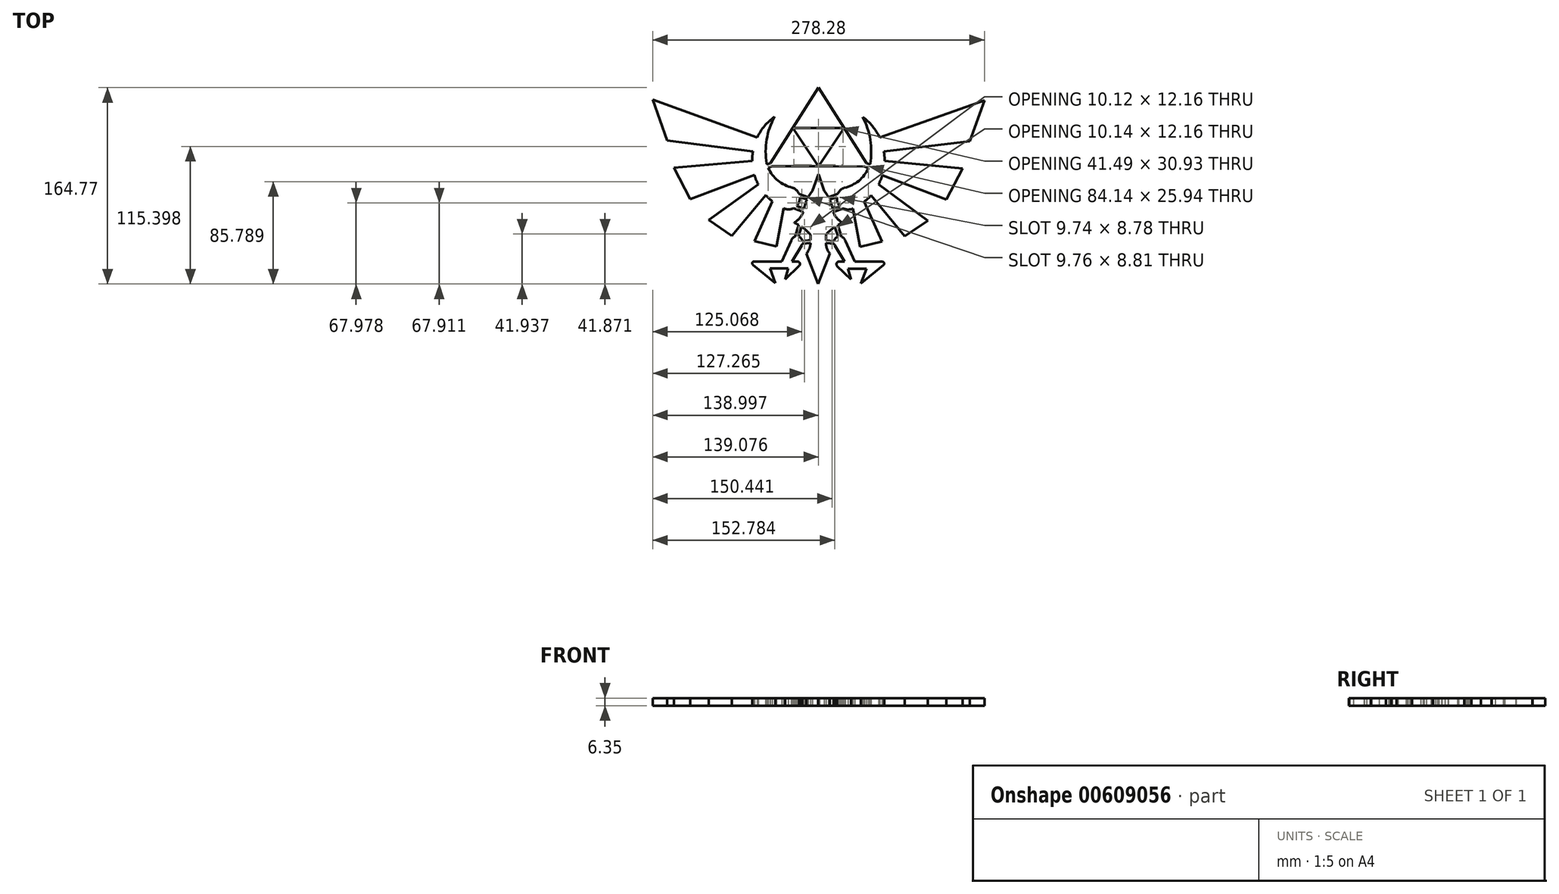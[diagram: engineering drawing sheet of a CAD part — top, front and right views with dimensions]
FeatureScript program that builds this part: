
annotation { "Feature Type Name" : "Feature", "Feature Type Description" : "" }
export const myFeature = defineFeature(function(context is Context, id is Id, definition is map)
    precondition{}
    {
        {
            var Q0;
            Q0=qCreatedBy(makeId("Top.planeOp"),FACE);
            var sketch = newSketch(context, id + "F0", { "sketchPlane" : qUnion([Q0])});
            skArc(sketch, "E0", {"start": v(-28.79, -20.12) * mm, "mid": v(-24.77, -21.01) * mm, "end": v(-20.76, -20.1) * mm});
            skLineSegment(sketch, "E1", {"start": v(-38.33, -14.34) * mm, "end": v(-53.53, -47.7) * mm});
            skLineSegment(sketch, "E2", {"start": v(-53.53, -47.7) * mm, "end": v(-35.08, -52.18) * mm});
            skLineSegment(sketch, "E3", {"start": v(-35.08, -52.18) * mm, "end": v(-28.79, -20.12) * mm});
            skLineSegment(sketch, "E4", {"start": v(-43.98, -9.01) * mm, "end": v(-72.5, -43.13) * mm});
            skLineSegment(sketch, "E5", {"start": v(-72.5, -43.13) * mm, "end": v(-91.8, -29.95) * mm});
            skLineSegment(sketch, "E6", {"start": v(-91.8, -29.95) * mm, "end": v(-50.28, 0.16) * mm});
            skLineSegment(sketch, "E7", {"start": v(-53.41, 7.92) * mm, "end": v(-107.23, -12.28) * mm});
            skLineSegment(sketch, "E8", {"start": v(-107.23, -12.28) * mm, "end": v(-120.85, 13.84) * mm});
            skLineSegment(sketch, "E9", {"start": v(-120.85, 13.84) * mm, "end": v(-55.26, 19.83) * mm});
            skLineSegment(sketch, "E10", {"start": v(-54.69, 27.79) * mm, "end": v(-126.62, 36.86) * mm});
            skLineSegment(sketch, "E11", {"start": v(-126.62, 36.86) * mm, "end": v(-138.76, 71.25) * mm});
            skLineSegment(sketch, "E12", {"start": v(-138.76, 71.25) * mm, "end": v(-51.03, 39.53) * mm});
            skArc(sketch, "E13", {"start": v(-36.63, 56.77) * mm, "mid": v(-44.94, 49.07) * mm, "end": v(-51.03, 39.53) * mm});
            skArc(sketch, "E14.trimOffspring", {"start": v(-54.69, 27.79) * mm, "mid": v(-55.16, 23.82) * mm, "end": v(-55.27, 19.83) * mm});
            skArc(sketch, "E15.trimOffspring", {"start": v(-53.44, 7.9) * mm, "mid": v(-52.06, 3.95) * mm, "end": v(-50.32, 0.14) * mm});
            skArc(sketch, "E16.trimOffspring", {"start": v(-44, -9.04) * mm, "mid": v(-41.29, -11.83) * mm, "end": v(-38.34, -14.37) * mm});
            skArc(sketch, "E17", {"start": v(-36.63, 56.77) * mm, "mid": v(-43.19, 37.67) * mm, "end": v(-43.16, 17.49) * mm});
            skArc(sketch, "E18", {"start": v(-43.16, 17.49) * mm, "mid": v(-43.09, 17.22) * mm, "end": v(-43, 16.96) * mm});
            skArc(sketch, "E19", {"start": v(-13.79, -50.98) * mm, "mid": v(-13.48, -50.39) * mm, "end": v(-13.26, -49.76) * mm});
            skLineSegment(sketch, "E20", {"start": v(-22.58, -47.14) * mm, "end": v(-30.59, -64.63) * mm});
            skLineSegment(sketch, "E21", {"start": v(-30.59, -64.63) * mm, "end": v(-53.76, -64.63) * mm});
            skLineSegment(sketch, "E22", {"start": v(-22.04, -64.63) * mm, "end": v(-17.52, -64.63) * mm});
            skLineSegment(sketch, "E23", {"start": v(-13.79, -50.98) * mm, "end": v(-22.04, -64.63) * mm});
            skArc(sketch, "E24", {"start": v(-53.47, -64.63) * mm, "mid": v(-55.2, -65.58) * mm, "end": v(-54.75, -67.5) * mm});
            skArc(sketch, "E25", {"start": v(-16.15, -68.69) * mm, "mid": v(-15.4, -66.17) * mm, "end": v(-17.52, -64.63) * mm});
            skLineSegment(sketch, "E26", {"start": v(-15.83, -68.38) * mm, "end": v(-27.53, -79.54) * mm});
            skLineSegment(sketch, "E27", {"start": v(-27.53, -79.54) * mm, "end": v(-25.03, -70.53) * mm});
            skLineSegment(sketch, "E28", {"start": v(-25.03, -70.53) * mm, "end": v(-40.41, -70.53) * mm});
            skLineSegment(sketch, "E29", {"start": v(-40.41, -70.53) * mm, "end": v(-35.86, -82.97) * mm});
            skLineSegment(sketch, "E30", {"start": v(-35.86, -82.97) * mm, "end": v(-54.75, -67.5) * mm});
            skLineSegment(sketch, "E31", {"start": v(0, 8.03) * mm, "end": v(-4.66, -5.48) * mm});
            skArc(sketch, "E32", {"start": v(-4.66, -5.48) * mm, "mid": v(-6.6, -8) * mm, "end": v(-8.28, -10.68) * mm});
            skArc(sketch, "E33", {"start": v(-20.17, -32.15) * mm, "mid": v(-15.52, -28.26) * mm, "end": v(-12.38, -23.07) * mm});
            skArc(sketch, "E34", {"start": v(-6.43, -42.15) * mm, "mid": v(-9.93, -38.58) * mm, "end": v(-13.88, -35.52) * mm});
            skArc(sketch, "E35", {"start": v(-9.73, -57.97) * mm, "mid": v(-7.47, -54.25) * mm, "end": v(-6.43, -50.01) * mm});
            skLineSegment(sketch, "E36", {"start": v(-6.43, -42.15) * mm, "end": v(-6.43, -46.8) * mm});
            skLineSegment(sketch, "E37", {"start": v(-9.73, -57.97) * mm, "end": v(0, -83.54) * mm});
            skLineSegment(sketch, "E38", {"start": v(-20.43, 46.05) * mm, "end": v(-0.78, 16.4) * mm});
            skLineSegment(sketch, "E39", {"start": v(0, 15.22) * mm, "end": v(-38.54, 15.22) * mm});
            skLineSegment(sketch, "E40", {"start": v(-40.13, 17.92) * mm, "end": v(-21.27, 47.32) * mm});
            skLineSegment(sketch, "E41", {"start": v(-21.27, 47.32) * mm, "end": v(0.4, 81.23) * mm});
            skLineSegment(sketch, "E42", {"start": v(-19.67, 47.32) * mm, "end": v(0, 47.32) * mm});
            skLineSegment(sketch, "E43", {"start": v(-16.07, -8) * mm, "end": v(-8.28, -10.68) * mm});
            skLineSegment(sketch, "E44", {"start": v(-15.4, -10.68) * mm, "end": v(-9.29, -12.65) * mm});
            skLineSegment(sketch, "E45", {"start": v(-18.1, -18.23) * mm, "end": v(-11.78, -20.44) * mm});
            skLineSegment(sketch, "E46", {"start": v(-20.76, -20.1) * mm, "end": v(-12.38, -23.07) * mm});
            skArc(sketch, "E47.trimOffspring", {"start": v(-16.07, -8) * mm, "mid": v(-18.29, -4.76) * mm, "end": v(-21.63, -2.7) * mm});
            skArc(sketch, "E48.trimOffspring", {"start": v(-9.29, -12.65) * mm, "mid": v(-10.79, -16.47) * mm, "end": v(-11.78, -20.44) * mm});
            skArc(sketch, "E49.trimOffspring", {"start": v(-18.1, -18.23) * mm, "mid": v(-15.9, -14.76) * mm, "end": v(-15.4, -10.68) * mm});
            skLineSegment(sketch, "E50", {"start": v(-19.52, -43.9) * mm, "end": v(-16.34, -34.01) * mm});
            skLineSegment(sketch, "E51", {"start": v(-16.56, -43.84) * mm, "end": v(-13.88, -35.52) * mm});
            skLineSegment(sketch, "E52", {"start": v(-13.15, -47.68) * mm, "end": v(-6.43, -46.8) * mm});
            skLineSegment(sketch, "E53", {"start": v(-13.26, -49.76) * mm, "end": v(-6.43, -49.06) * mm});
            skArc(sketch, "E54.trimOffspring", {"start": v(-13.15, -47.68) * mm, "mid": v(-14.3, -45.27) * mm, "end": v(-16.56, -43.84) * mm});
            skLineSegment(sketch, "E55.trimOffspring", {"start": v(-6.43, -49.06) * mm, "end": v(-6.43, -50.01) * mm});
            skArc(sketch, "E56.trimOffspring", {"start": v(-19.52, -43.9) * mm, "mid": v(-21.44, -45.15) * mm, "end": v(-22.58, -47.14) * mm});
            skArc(sketch, "E57.trimOffspring", {"start": v(-16.34, -34.01) * mm, "mid": v(-18.22, -33.03) * mm, "end": v(-20.17, -32.15) * mm});
            skLineSegment(sketch, "E58", {"start": v(-40.13, 17.92) * mm, "end": v(-43, 16.96) * mm});
            skLineSegment(sketch, "E59", {"start": v(-38.54, 15.22) * mm, "end": v(-41.83, 13.84) * mm});
            skArc(sketch, "E60.trimOffspring", {"start": v(-41.83, 13.84) * mm, "mid": v(-33.7, 3.16) * mm, "end": v(-21.63, -2.7) * mm});
            skLineSegment(sketch, "E61", {"start": v(-20.43, 46.05) * mm, "end": v(-19.67, 47.32) * mm});
            skLineSegment(sketch, "E62.MirrorCS", {"start": v(6.6, -49.09) * mm, "end": v(6.6, -50.04) * mm});
            skArc(sketch, "E63.MirrorCS", {"start": v(43.66, 17.27) * mm, "mid": v(43.58, 17.01) * mm, "end": v(43.5, 16.75) * mm});
            skLineSegment(sketch, "E64.MirrorCS", {"start": v(40.62, 17.73) * mm, "end": v(43.5, 16.75) * mm});
            skLineSegment(sketch, "E65.MirrorCS", {"start": v(13.43, -49.83) * mm, "end": v(6.6, -49.09) * mm});
            skArc(sketch, "E66.MirrorCS", {"start": v(13.94, -51.05) * mm, "mid": v(13.64, -50.45) * mm, "end": v(13.43, -49.83) * mm});
            skLineSegment(sketch, "E67.MirrorCS", {"start": v(13.33, -47.75) * mm, "end": v(6.61, -46.83) * mm});
            skArc(sketch, "E68.MirrorCS", {"start": v(16.44, -8.08) * mm, "mid": v(18.67, -4.85) * mm, "end": v(22.03, -2.81) * mm});
            skLineSegment(sketch, "E69.MirrorCS", {"start": v(22.13, -64.74) * mm, "end": v(17.61, -64.72) * mm});
            skArc(sketch, "E70.MirrorCS", {"start": v(13.33, -47.75) * mm, "mid": v(14.49, -45.34) * mm, "end": v(16.75, -43.92) * mm});
            skLineSegment(sketch, "E71.MirrorCS", {"start": v(15.76, -10.76) * mm, "end": v(9.63, -12.7) * mm});
            skArc(sketch, "E72.MirrorCS", {"start": v(6.64, -42.19) * mm, "mid": v(10.15, -38.63) * mm, "end": v(14.12, -35.59) * mm});
            skLineSegment(sketch, "E73.MirrorCS", {"start": v(6.64, -42.19) * mm, "end": v(6.61, -46.83) * mm});
            skArc(sketch, "E74.MirrorCS", {"start": v(19.71, -44) * mm, "mid": v(21.63, -45.26) * mm, "end": v(22.76, -47.25) * mm});
            skArc(sketch, "E75.MirrorCS", {"start": v(53.56, -64.9) * mm, "mid": v(55.3, -65.85) * mm, "end": v(54.82, -67.77) * mm});
            skLineSegment(sketch, "E76.MirrorCS", {"start": v(39.03, 15.03) * mm, "end": v(42.3, 13.63) * mm});
            skLineSegment(sketch, "E77.MirrorCS", {"start": v(16.44, -8.08) * mm, "end": v(8.63, -10.72) * mm});
            skLineSegment(sketch, "E78.MirrorCS", {"start": v(21.06, 45.95) * mm, "end": v(20.3, 47.23) * mm});
            skArc(sketch, "E79.MirrorCS", {"start": v(16.22, -68.77) * mm, "mid": v(15.48, -66.25) * mm, "end": v(17.61, -64.72) * mm});
            skLineSegment(sketch, "E80.MirrorCS", {"start": v(18.41, -18.31) * mm, "end": v(12.1, -20.5) * mm});
            skArc(sketch, "E81.MirrorCS", {"start": v(44.37, -9.25) * mm, "mid": v(41.64, -12.03) * mm, "end": v(38.68, -14.55) * mm});
            skArc(sketch, "E82.MirrorCS", {"start": v(5.04, -5.5) * mm, "mid": v(6.97, -8.02) * mm, "end": v(8.63, -10.72) * mm});
            skArc(sketch, "E83.MirrorCS", {"start": v(16.58, -34.1) * mm, "mid": v(18.47, -33.12) * mm, "end": v(20.42, -32.25) * mm});
            skArc(sketch, "E84.MirrorCS", {"start": v(37.32, 56.59) * mm, "mid": v(45.59, 48.85) * mm, "end": v(51.63, 39.28) * mm});
            skLineSegment(sketch, "E85.MirrorCS", {"start": v(0.45, 8.03) * mm, "end": v(5.04, -5.5) * mm});
            skArc(sketch, "E86.MirrorCS", {"start": v(55.23, 27.52) * mm, "mid": v(55.68, 23.55) * mm, "end": v(55.78, 19.56) * mm});
            skLineSegment(sketch, "E87.MirrorCS", {"start": v(21.06, 45.95) * mm, "end": v(1.27, 16.4) * mm});
            skArc(sketch, "E88.MirrorCS", {"start": v(53.89, 7.64) * mm, "mid": v(52.49, 3.7) * mm, "end": v(50.72, -0.1) * mm});
            skArc(sketch, "E89.MirrorCS", {"start": v(29.1, -20.26) * mm, "mid": v(25.08, -21.13) * mm, "end": v(21.07, -20.21) * mm});
            skLineSegment(sketch, "E90.MirrorCS", {"start": v(38.67, -14.53) * mm, "end": v(53.7, -47.96) * mm});
            skLineSegment(sketch, "E91.MirrorCS", {"start": v(53.7, -47.96) * mm, "end": v(35.23, -52.36) * mm});
            skLineSegment(sketch, "E92.MirrorCS", {"start": v(35.23, -52.36) * mm, "end": v(29.1, -20.26) * mm});
            skLineSegment(sketch, "E93.MirrorCS", {"start": v(44.35, -9.23) * mm, "end": v(72.69, -43.49) * mm});
            skLineSegment(sketch, "E94.MirrorCS", {"start": v(72.69, -43.49) * mm, "end": v(92.06, -30.4) * mm});
            skLineSegment(sketch, "E95.MirrorCS", {"start": v(9.85, -58.02) * mm, "end": v(0, -83.54) * mm});
            skLineSegment(sketch, "E96.MirrorCS", {"start": v(35.86, -83.14) * mm, "end": v(54.82, -67.77) * mm});
            skLineSegment(sketch, "E97.MirrorCS", {"start": v(21.07, -20.21) * mm, "end": v(12.67, -23.14) * mm});
            skLineSegment(sketch, "E98.MirrorCS", {"start": v(30.68, -64.78) * mm, "end": v(53.85, -64.9) * mm});
            skLineSegment(sketch, "E99.MirrorCS", {"start": v(25.1, -70.65) * mm, "end": v(40.48, -70.73) * mm});
            skArc(sketch, "E100.MirrorCS", {"start": v(42.3, 13.63) * mm, "mid": v(34.13, 3) * mm, "end": v(22.03, -2.81) * mm});
            skLineSegment(sketch, "E101.MirrorCS", {"start": v(92.06, -30.4) * mm, "end": v(50.7, -0.08) * mm});
            skLineSegment(sketch, "E102.MirrorCS", {"start": v(53.86, 7.65) * mm, "end": v(107.57, -12.8) * mm});
            skLineSegment(sketch, "E103.MirrorCS", {"start": v(107.57, -12.8) * mm, "end": v(121.32, 13.25) * mm});
            skLineSegment(sketch, "E104.MirrorCS", {"start": v(121.32, 13.25) * mm, "end": v(55.76, 19.56) * mm});
            skLineSegment(sketch, "E105.MirrorCS", {"start": v(55.23, 27.52) * mm, "end": v(127.2, 36.24) * mm});
            skLineSegment(sketch, "E106.MirrorCS", {"start": v(127.2, 36.24) * mm, "end": v(139.52, 70.57) * mm});
            skLineSegment(sketch, "E107.MirrorCS", {"start": v(139.52, 70.57) * mm, "end": v(51.63, 39.28) * mm});
            skLineSegment(sketch, "E108.MirrorCS", {"start": v(0.48, 15.22) * mm, "end": v(39.03, 15.03) * mm});
            skLineSegment(sketch, "E109.MirrorCS", {"start": v(13.94, -51.05) * mm, "end": v(22.13, -64.74) * mm});
            skLineSegment(sketch, "E110.MirrorCS", {"start": v(20.3, 47.23) * mm, "end": v(0.64, 47.32) * mm});
            skLineSegment(sketch, "E111.MirrorCS", {"start": v(21.91, 47.22) * mm, "end": v(0.4, 81.23) * mm});
            skLineSegment(sketch, "E112.MirrorCS", {"start": v(40.62, 17.73) * mm, "end": v(21.91, 47.22) * mm});
            skLineSegment(sketch, "E113.MirrorCS", {"start": v(19.71, -44) * mm, "end": v(16.58, -34.1) * mm});
            skLineSegment(sketch, "E114.MirrorCS", {"start": v(27.55, -79.68) * mm, "end": v(25.1, -70.65) * mm});
            skArc(sketch, "E115.MirrorCS", {"start": v(20.42, -32.25) * mm, "mid": v(15.8, -28.33) * mm, "end": v(12.67, -23.14) * mm});
            skLineSegment(sketch, "E116.MirrorCS", {"start": v(22.76, -47.25) * mm, "end": v(30.68, -64.78) * mm});
            skArc(sketch, "E117.MirrorCS", {"start": v(9.63, -12.7) * mm, "mid": v(11.11, -16.52) * mm, "end": v(12.1, -20.5) * mm});
            skLineSegment(sketch, "E118.MirrorCS", {"start": v(15.9, -68.46) * mm, "end": v(27.55, -79.68) * mm});
            skArc(sketch, "E119.MirrorCS", {"start": v(37.32, 56.59) * mm, "mid": v(43.78, 37.46) * mm, "end": v(43.66, 17.27) * mm});
            skLineSegment(sketch, "E120.MirrorCS", {"start": v(16.75, -43.92) * mm, "end": v(14.12, -35.59) * mm});
            skLineSegment(sketch, "E121.MirrorCS", {"start": v(40.48, -70.73) * mm, "end": v(35.86, -83.14) * mm});
            skArc(sketch, "E122.MirrorCS", {"start": v(9.85, -58.02) * mm, "mid": v(7.61, -54.28) * mm, "end": v(6.6, -50.04) * mm});
            skArc(sketch, "E123.MirrorCS", {"start": v(18.41, -18.31) * mm, "mid": v(16.24, -14.83) * mm, "end": v(15.76, -10.76) * mm});
            skLineSegment(sketch, "E124", {"start": v(0, 15.22) * mm, "end": v(0.48, 15.22) * mm});
            skLineSegment(sketch, "E125", {"start": v(-0.78, 16.4) * mm, "end": v(1.27, 16.4) * mm});
            skLineSegment(sketch, "E126", {"start": v(0, 47.32) * mm, "end": v(0.64, 47.32) * mm});
            skLineSegment(sketch, "E127", {"start": v(0, 8.03) * mm, "end": v(0.21, 8.64) * mm});
            skLineSegment(sketch, "E128", {"start": v(0.45, 8.03) * mm, "end": v(0.21, 8.64) * mm});
            skSolve(sketch);
        }
        {
            var Q0;
            Q0=makeQuery(id+"F0.imprint","IMPRINT",FACE,{"disambiguationData":[TD([[makeQuery(id+"F0.imprint","IMPRINT",EDGE,{"derivedFrom":sQuery(id+"F0.wireOp",EDGE,"E0")}),1.0]])]});
            extrude(context, id + "F1", {"entities" : qUnion([Q0]), "depth" : 6.35 * mm, "offsetDistance" : 25.4 * mm});
        }
    });
